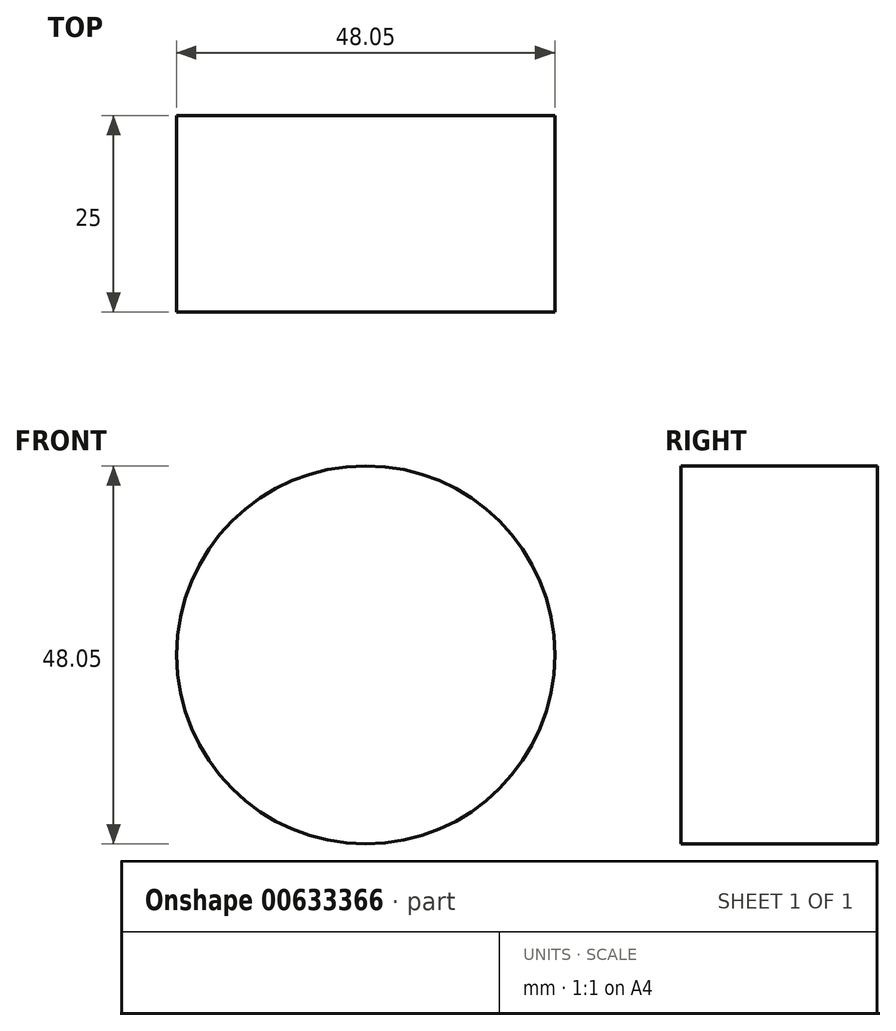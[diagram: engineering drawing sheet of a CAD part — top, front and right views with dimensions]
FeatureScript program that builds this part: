
annotation { "Feature Type Name" : "Feature", "Feature Type Description" : "" }
export const myFeature = defineFeature(function(context is Context, id is Id, definition is map)
    precondition{}
    {
        {
            var Q0;
            Q0=qCreatedBy(makeId("Front.planeOp"),FACE);
            var sketch = newSketch(context, id + "F0", { "sketchPlane" : qUnion([Q0])});
            skCircle(sketch, "E0", {"center": v(-47.77, 36.15) * mm, "radius": 24.02 * mm});
            skPoint(sketch, "E1", {"position": v(-28.92, 21.25) * mm});
            skSolve(sketch);
        }
        {
            var Q0;
            Q0=makeQuery(id+"F0.imprint","IMPRINT",FACE,{"disambiguationData":[TD([[makeQuery(id+"F0.imprint","IMPRINT",EDGE,{"derivedFrom":sQuery(id+"F0.wireOp",EDGE,"E0")}),1.0]])]});
            extrude(context, id + "F1", {"entities" : qUnion([Q0]), "depth" : 25 * mm, "offsetDistance" : 25 * mm});
        }
    });
